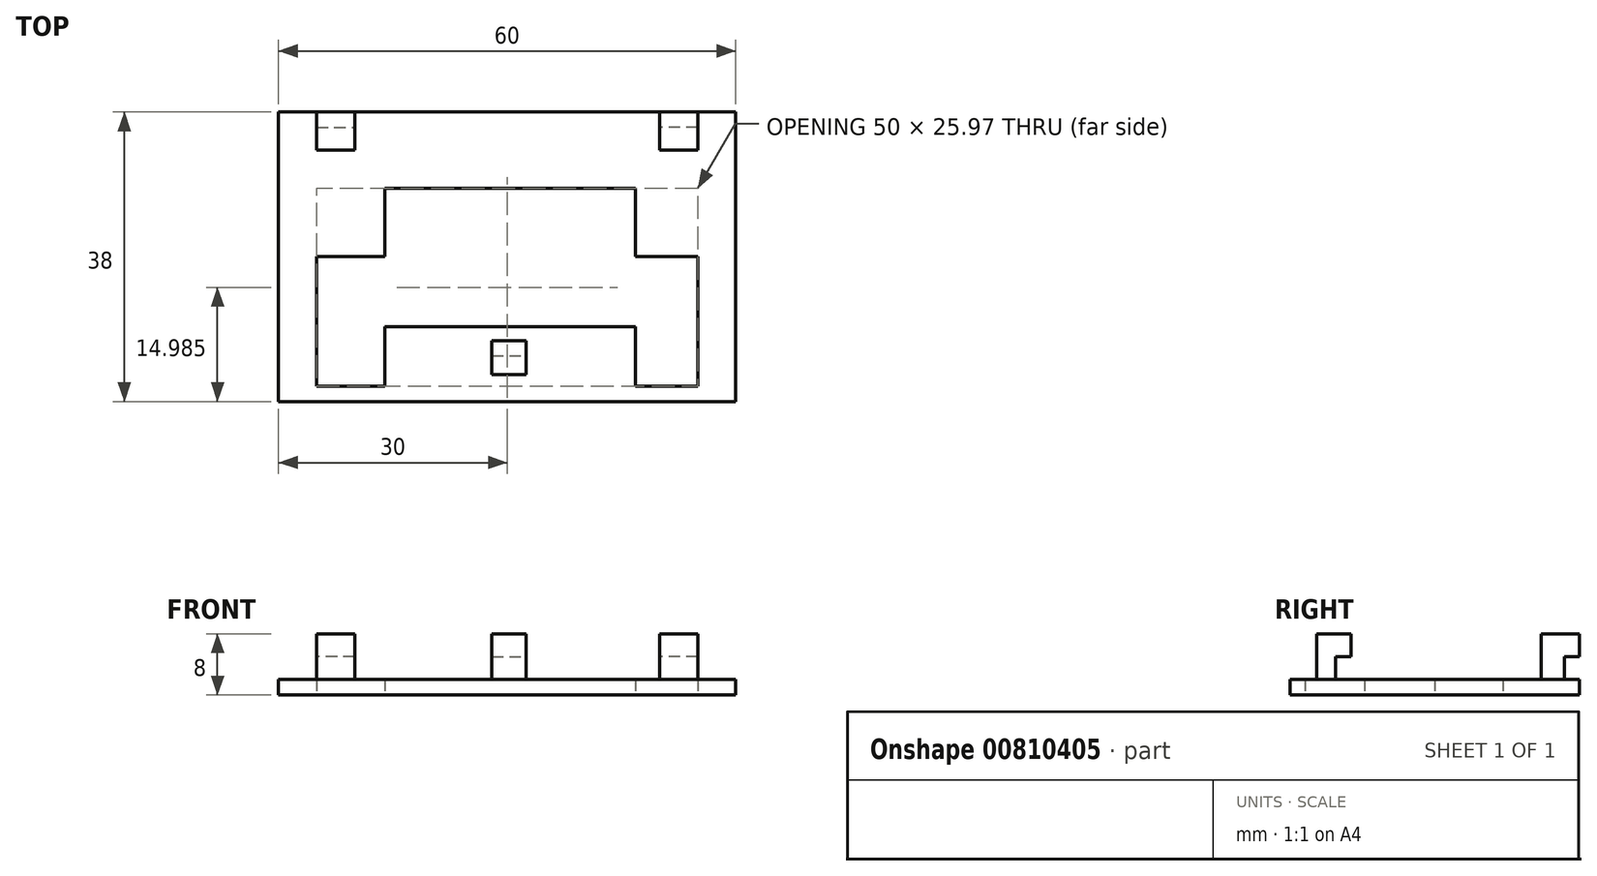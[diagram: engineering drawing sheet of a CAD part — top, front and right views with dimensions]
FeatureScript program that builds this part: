
annotation { "Feature Type Name" : "Feature", "Feature Type Description" : "" }
export const myFeature = defineFeature(function(context is Context, id is Id, definition is map)
    precondition{}
    {
        {
            var Q0;
            Q0=qCreatedBy(makeId("Top.planeOp"),FACE);
            var sketch = newSketch(context, id + "F0", { "sketchPlane" : qUnion([Q0])});
            skPoint(sketch, "E0.middle", {"position": v(0, 0) * mm});
            skLineSegment(sketch, "E1.bottom", {"start": v(-25, 17) * mm, "end": v(25, 17) * mm, "construction": true});
            skLineSegment(sketch, "E1.top", {"start": v(-25, -17) * mm, "end": v(25, -17) * mm, "construction": true});
            skLineSegment(sketch, "E1.left", {"start": v(-25, 17) * mm, "end": v(-25, -17) * mm, "construction": true});
            skLineSegment(sketch, "E1.right", {"start": v(25, 17) * mm, "end": v(25, -17) * mm, "construction": true});
            skLineSegment(sketch, "E2.bottom", {"start": v(-25, 17) * mm, "end": v(-20, 17) * mm});
            skLineSegment(sketch, "E2.top", {"start": v(-25, 14) * mm, "end": v(-20, 14) * mm});
            skLineSegment(sketch, "E2.left", {"start": v(-25, 17) * mm, "end": v(-25, 14) * mm});
            skLineSegment(sketch, "E2.right", {"start": v(-20, 17) * mm, "end": v(-20, 14) * mm});
            skLineSegment(sketch, "E3.bottom", {"start": v(25, 17) * mm, "end": v(20, 17) * mm});
            skLineSegment(sketch, "E3.top", {"start": v(25, 14) * mm, "end": v(20, 14) * mm});
            skLineSegment(sketch, "E3.left", {"start": v(25, 17) * mm, "end": v(25, 14) * mm});
            skLineSegment(sketch, "E3.right", {"start": v(20, 17) * mm, "end": v(20, 14) * mm});
            skPoint(sketch, "E4.middle", {"position": v(0, -17) * mm});
            skLineSegment(sketch, "E5", {"start": v(-2, -15.5) * mm, "end": v(2.5, -15.5) * mm});
            skLineSegment(sketch, "E6.bottom", {"start": v(-30, 19) * mm, "end": v(30, 19) * mm});
            skLineSegment(sketch, "E6.top", {"start": v(-30, -19) * mm, "end": v(30, -19) * mm});
            skLineSegment(sketch, "E6.left", {"start": v(-30, 19) * mm, "end": v(-30, -19) * mm});
            skLineSegment(sketch, "E6.right", {"start": v(30, 19) * mm, "end": v(30, -19) * mm});
            skLineSegment(sketch, "E7.bottom", {"start": v(-16.07, 8.97) * mm, "end": v(16.83, 8.97) * mm});
            skLineSegment(sketch, "E7.top", {"start": v(-16.07, -9.2) * mm, "end": v(16.83, -9.2) * mm});
            skLineSegment(sketch, "E7.left", {"start": v(-16.07, 8.97) * mm, "end": v(-16.07, -9.2) * mm});
            skLineSegment(sketch, "E7.right", {"start": v(16.83, 8.97) * mm, "end": v(16.83, -9.2) * mm});
            skLineSegment(sketch, "E8.bottom", {"start": v(-16.07, 0) * mm, "end": v(-25, 0) * mm});
            skLineSegment(sketch, "E8.top", {"start": v(-16.07, -17) * mm, "end": v(-25, -17) * mm});
            skLineSegment(sketch, "E8.left", {"start": v(-16.07, 0) * mm, "end": v(-16.07, -17) * mm});
            skLineSegment(sketch, "E8.right", {"start": v(-25, 0) * mm, "end": v(-25, -17) * mm});
            skLineSegment(sketch, "E9.bottom", {"start": v(16.83, 0) * mm, "end": v(25, 0) * mm});
            skLineSegment(sketch, "E9.top", {"start": v(16.83, -17) * mm, "end": v(25, -17) * mm});
            skLineSegment(sketch, "E9.left", {"start": v(16.83, 0) * mm, "end": v(16.83, -17) * mm});
            skLineSegment(sketch, "E9.right", {"start": v(25, 0) * mm, "end": v(25, -17) * mm});
            skLineSegment(sketch, "E10", {"start": v(2.5, -15.5) * mm, "end": v(2.5, -13) * mm});
            skLineSegment(sketch, "E11", {"start": v(-2, -15.5) * mm, "end": v(-2, -13) * mm});
            skLineSegment(sketch, "E12", {"start": v(-2, -13) * mm, "end": v(2.5, -13) * mm});
            skSolve(sketch);
        }
        {
            var Q0;
            Q0=makeQuery(id+"F0.imprint","IMPRINT",FACE,{"disambiguationData":[TD([[makeQuery(id+"F0.imprint","IMPRINT",EDGE,{"derivedFrom":sQuery(id+"F0.wireOp",EDGE,"E2.bottom")}),1.0]])]});
            extrude(context, id + "F1", {"entities" : qUnion([Q0]), "depth" : 2 * mm, "offsetDistance" : 25 * mm});
        }
        {
            var Q0;
            Q0=makeQuery(id+"F0.imprint","IMPRINT",FACE,{"disambiguationData":[TD([[makeQuery(id+"F0.imprint","IMPRINT",EDGE,{"derivedFrom":sQuery(id+"F0.wireOp",EDGE,"E3.bottom")}),1.0]])]});
            var Q1;
            Q1=makeQuery(id+"F0.imprint","IMPRINT",FACE,{"disambiguationData":[TD([[makeQuery(id+"F0.imprint","IMPRINT",EDGE,{"derivedFrom":sQuery(id+"F0.wireOp",EDGE,"E4.bottom")}),-1.0]])]});
            var Q2;
            Q2=makeQuery(id+"F0.imprint","IMPRINT",FACE,{"disambiguationData":[TD([[makeQuery(id+"F0.imprint","IMPRINT",EDGE,{"derivedFrom":sQuery(id+"F0.wireOp",EDGE,"E2.bottom")}),-1.0]])]});
            extrude(context, id + "F2", {"entities" : qUnion([Q0, Q1, Q2]), "operationType" : NewBodyOperationType.ADD, "depth" : 8 * mm, "offsetDistance" : 25 * mm});
        }
        {
            var Q0;
            Q0=makeQuery(id+"F2.opExtrude","SWEPT_FACE",FACE,{"disambiguationData":[OSD([sQuery(id+"F0.wireOp",EDGE,"E2.bottom")])]});
            var sketch = newSketch(context, id + "F3", { "sketchPlane" : qUnion([Q0])});
            skLineSegment(sketch, "E13.bottom", {"start": v(20, 8) * mm, "end": v(25, 8) * mm});
            skLineSegment(sketch, "E13.top", {"start": v(20, 5) * mm, "end": v(25, 5) * mm});
            skLineSegment(sketch, "E13.left", {"start": v(20, 8) * mm, "end": v(20, 5) * mm});
            skLineSegment(sketch, "E13.right", {"start": v(25, 8) * mm, "end": v(25, 5) * mm});
            skSolve(sketch);
        }
        {
            var Q0;
            Q0 = qSketchRegion(id + "F3", true);
            extrude(context, id + "F4", {"entities" : qUnion([Q0]), "operationType" : NewBodyOperationType.ADD, "depth" : 2 * mm, "offsetDistance" : 25 * mm});
        }
        {
            var Q0;
            Q0=makeQuery(id+"F2.opExtrude","SWEPT_FACE",FACE,{"disambiguationData":[OSD([sQuery(id+"F0.wireOp",EDGE,"E3.bottom")])]});
            var sketch = newSketch(context, id + "F5", { "sketchPlane" : qUnion([Q0])});
            skLineSegment(sketch, "E14.bottom", {"start": v(-25, 8) * mm, "end": v(-20, 8) * mm});
            skLineSegment(sketch, "E14.top", {"start": v(-25, 5) * mm, "end": v(-20, 5) * mm});
            skLineSegment(sketch, "E14.left", {"start": v(-25, 8) * mm, "end": v(-25, 5) * mm});
            skLineSegment(sketch, "E14.right", {"start": v(-20, 8) * mm, "end": v(-20, 5) * mm});
            skSolve(sketch);
        }
        {
            var Q0;
            Q0 = qSketchRegion(id + "F5", true);
            extrude(context, id + "F6", {"entities" : qUnion([Q0]), "operationType" : NewBodyOperationType.ADD, "depth" : 2 * mm, "offsetDistance" : 25 * mm});
        }
        {
            var Q0;
            Q0=makeQuery(id+"F0.imprint","IMPRINT",FACE,{"disambiguationData":[TD([[makeQuery(id+"F0.imprint","IMPRINT",EDGE,{"derivedFrom":sQuery(id+"F0.wireOp",EDGE,"E5")}),1.0]])]});
            extrude(context, id + "F7", {"entities" : qUnion([Q0]), "operationType" : NewBodyOperationType.ADD, "depth" : 8 * mm, "offsetDistance" : 25 * mm});
        }
        {
            var Q0;
            Q0=makeQuery(id+"F7.opExtrude","SWEPT_FACE",FACE,{"disambiguationData":[OSD([sQuery(id+"F0.wireOp",EDGE,"E12")])]});
            var sketch = newSketch(context, id + "F8", { "sketchPlane" : qUnion([Q0])});
            skLineSegment(sketch, "E15.bottom", {"start": v(2, 8) * mm, "end": v(-2.5, 8) * mm});
            skLineSegment(sketch, "E15.top", {"start": v(2, 5) * mm, "end": v(-2.5, 5) * mm});
            skLineSegment(sketch, "E15.left", {"start": v(2, 8) * mm, "end": v(2, 5) * mm});
            skLineSegment(sketch, "E15.right", {"start": v(-2.5, 8) * mm, "end": v(-2.5, 5) * mm});
            skSolve(sketch);
        }
        {
            var Q0;
            Q0 = qSketchRegion(id + "F8", true);
            extrude(context, id + "F9", {"entities" : qUnion([Q0]), "operationType" : NewBodyOperationType.ADD, "depth" : 2 * mm, "offsetDistance" : 25 * mm});
        }
    });
